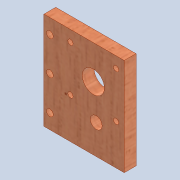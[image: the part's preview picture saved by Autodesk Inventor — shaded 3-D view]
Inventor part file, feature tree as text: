
AUTODESK INVENTOR PART (.ipt)
format: ipt  version: 2020 (Build 240168000, 168)  size: 283,648 bytes
history: native  units: mm
features: sketch x4, extrude x3, hole x1
ambient origin geometry x8: Origin, YZ Plane, XZ Plane, XY Plane, X Axis, Y Axis, Z Axis, Center Point
bodies: Solid1 (feature_tree)
feature tree (8):
  extrude  "Extrusion1"  Depth=66.0mm
  extrude  "Extrusion2"  TaperAngle=0.0deg  [1 undecoded]
  extrude  "Extrusion4"  Depth=21.0mm
  hole  "Hole1"  [1 undecoded]
  sketch  "Sketch1"  dims[d0=54.5mm d1=66.0mm]
  sketch  "Sketch2"  dims[d2=8.0mm d3=0.0mm d6=0.0mm d7=0.0mm]
  sketch  "Sketch4"  dims[d17=15.0mm d19=21.0mm]
  sketch  "Sketch5"  dims[d20=23.0mm d22=31.0mm d23=3.5mm d24=8.0mm d25=20.0mm d26=19.030905mm d27=0.0mm d28=0.0mm d29=4.0mm d30=23.0mm d31=23.0mm d32=4.5mm d33=6.0mm d34=4.0mm d35=2.0mm d36=90.0deg d37=8.0mm d38=20.594885mm]
note: 2 required parameter values undecoded (feature->parameter linkage not recoverable at this tier; creation-order binding heuristic only, values carry confidence <= 0.55)
